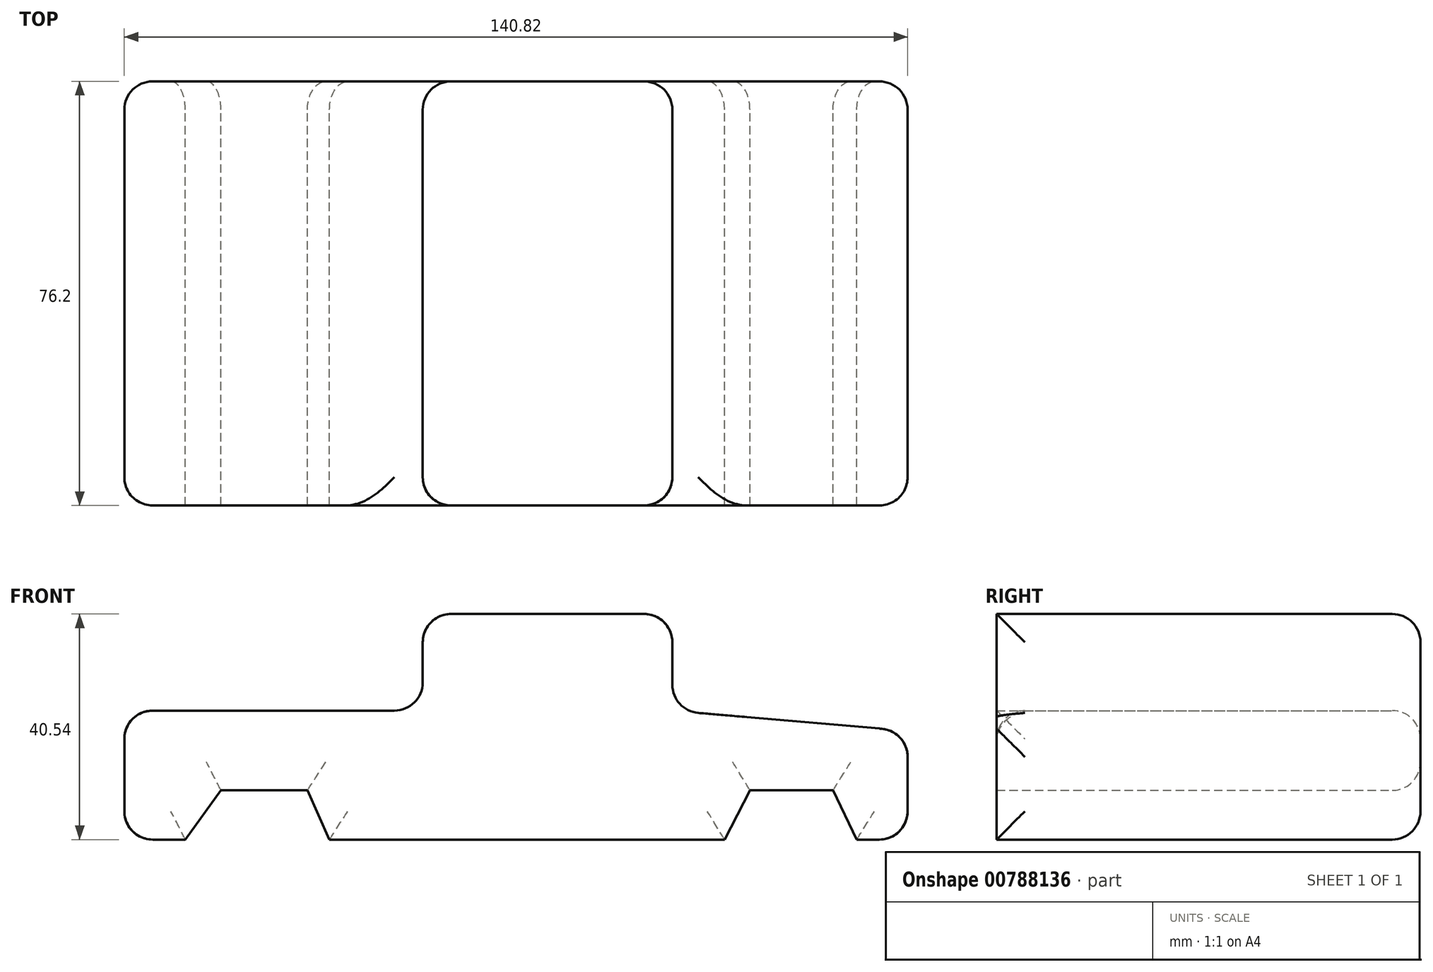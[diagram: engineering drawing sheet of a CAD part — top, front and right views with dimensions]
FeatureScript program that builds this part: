
annotation { "Feature Type Name" : "Feature", "Feature Type Description" : "" }
export const myFeature = defineFeature(function(context is Context, id is Id, definition is map)
    precondition{}
    {
        {
            var Q0;
            Q0=qCreatedBy(makeId("Front.planeOp"),FACE);
            var sketch = newSketch(context, id + "F0", { "sketchPlane" : qUnion([Q0])});
            skLineSegment(sketch, "E0", {"start": v(-98.53, 10.06) * mm, "end": v(-98.53, -13.1) * mm});
            skLineSegment(sketch, "E1", {"start": v(-98.53, 10.06) * mm, "end": v(-44.88, 10.06) * mm});
            skLineSegment(sketch, "E2", {"start": v(-44.88, 10.06) * mm, "end": v(-44.88, 27.43) * mm});
            skLineSegment(sketch, "E3", {"start": v(-44.88, 27.43) * mm, "end": v(0, 27.43) * mm});
            skLineSegment(sketch, "E4", {"start": v(0, 27.43) * mm, "end": v(0, 10.06) * mm});
            skLineSegment(sketch, "E5", {"start": v(0, 10.06) * mm, "end": v(42.3, 6.4) * mm});
            skLineSegment(sketch, "E6", {"start": v(42.3, 6.4) * mm, "end": v(42.3, -13.1) * mm});
            skLineSegment(sketch, "E7", {"start": v(-98.53, -13.1) * mm, "end": v(-87.55, -13.1) * mm});
            skLineSegment(sketch, "E8", {"start": v(-87.55, -13.1) * mm, "end": v(-81.15, -4.27) * mm});
            skLineSegment(sketch, "E9", {"start": v(-81.15, -4.27) * mm, "end": v(-65.6, -4.27) * mm});
            skLineSegment(sketch, "E10", {"start": v(-65.6, -4.27) * mm, "end": v(-61.65, -13.1) * mm});
            skLineSegment(sketch, "E11", {"start": v(-61.65, -13.1) * mm, "end": v(9.37, -13.1) * mm});
            skLineSegment(sketch, "E12", {"start": v(9.37, -13.1) * mm, "end": v(13.94, -4.27) * mm});
            skLineSegment(sketch, "E13", {"start": v(13.94, -4.27) * mm, "end": v(28.88, -4.27) * mm});
            skLineSegment(sketch, "E14", {"start": v(28.88, -4.27) * mm, "end": v(33.15, -13.1) * mm});
            skLineSegment(sketch, "E15", {"start": v(33.15, -13.1) * mm, "end": v(42.3, -13.1) * mm});
            skSolve(sketch);
        }
        {
            var Q0;
            Q0 = qSketchRegion(id + "F0", true);
            extrude(context, id + "F1", {"entities" : qUnion([Q0]), "endBound" : BoundingType.SYMMETRIC, "depth" : 76.2 * mm, "offsetDistance" : 25.4 * mm});
        }
        {
            var Q0;
            Q0=makeQuery(id+"F1.opExtrude","CAP_FACE",FACE,{"disambiguationData":[OSD([sQuery(id+"F0.wireOp",EDGE,"E0"),sQuery(id+"F0.wireOp",EDGE,"E1"),sQuery(id+"F0.wireOp",EDGE,"E2"),sQuery(id+"F0.wireOp",EDGE,"E3"),sQuery(id+"F0.wireOp",EDGE,"E4"),sQuery(id+"F0.wireOp",EDGE,"E5"),sQuery(id+"F0.wireOp",EDGE,"E6"),sQuery(id+"F0.wireOp",EDGE,"E7"),sQuery(id+"F0.wireOp",EDGE,"E8"),sQuery(id+"F0.wireOp",EDGE,"E9"),sQuery(id+"F0.wireOp",EDGE,"E10"),sQuery(id+"F0.wireOp",EDGE,"E11"),sQuery(id+"F0.wireOp",EDGE,"E12"),sQuery(id+"F0.wireOp",EDGE,"E13"),sQuery(id+"F0.wireOp",EDGE,"E14"),sQuery(id+"F0.wireOp",EDGE,"E15")])],"isStart":true});
            var Q1;
            Q1=makeQuery(id+"F1.opExtrude","SWEPT_FACE",FACE,{"disambiguationData":[OSD([sQuery(id+"F0.wireOp",EDGE,"E0")])]});
            var Q2;
            Q2=makeQuery(id+"F1.opExtrude","SWEPT_FACE",FACE,{"disambiguationData":[OSD([sQuery(id+"F0.wireOp",EDGE,"E2")])]});
            var Q3;
            Q3=makeQuery(id+"F1.opExtrude","SWEPT_FACE",FACE,{"disambiguationData":[OSD([sQuery(id+"F0.wireOp",EDGE,"E4")])]});
            var Q4;
            Q4=makeQuery(id+"F1.opExtrude","SWEPT_FACE",FACE,{"disambiguationData":[OSD([sQuery(id+"F0.wireOp",EDGE,"E6")])]});
            fillet(context, id + "F2", {"entities" : qUnion([Q0, Q1, Q2, Q3, Q4]), "radius" : 5.08 * mm, "tangentPropagation" : true, "allowEdgeOverflow" : false});
        }
    });
